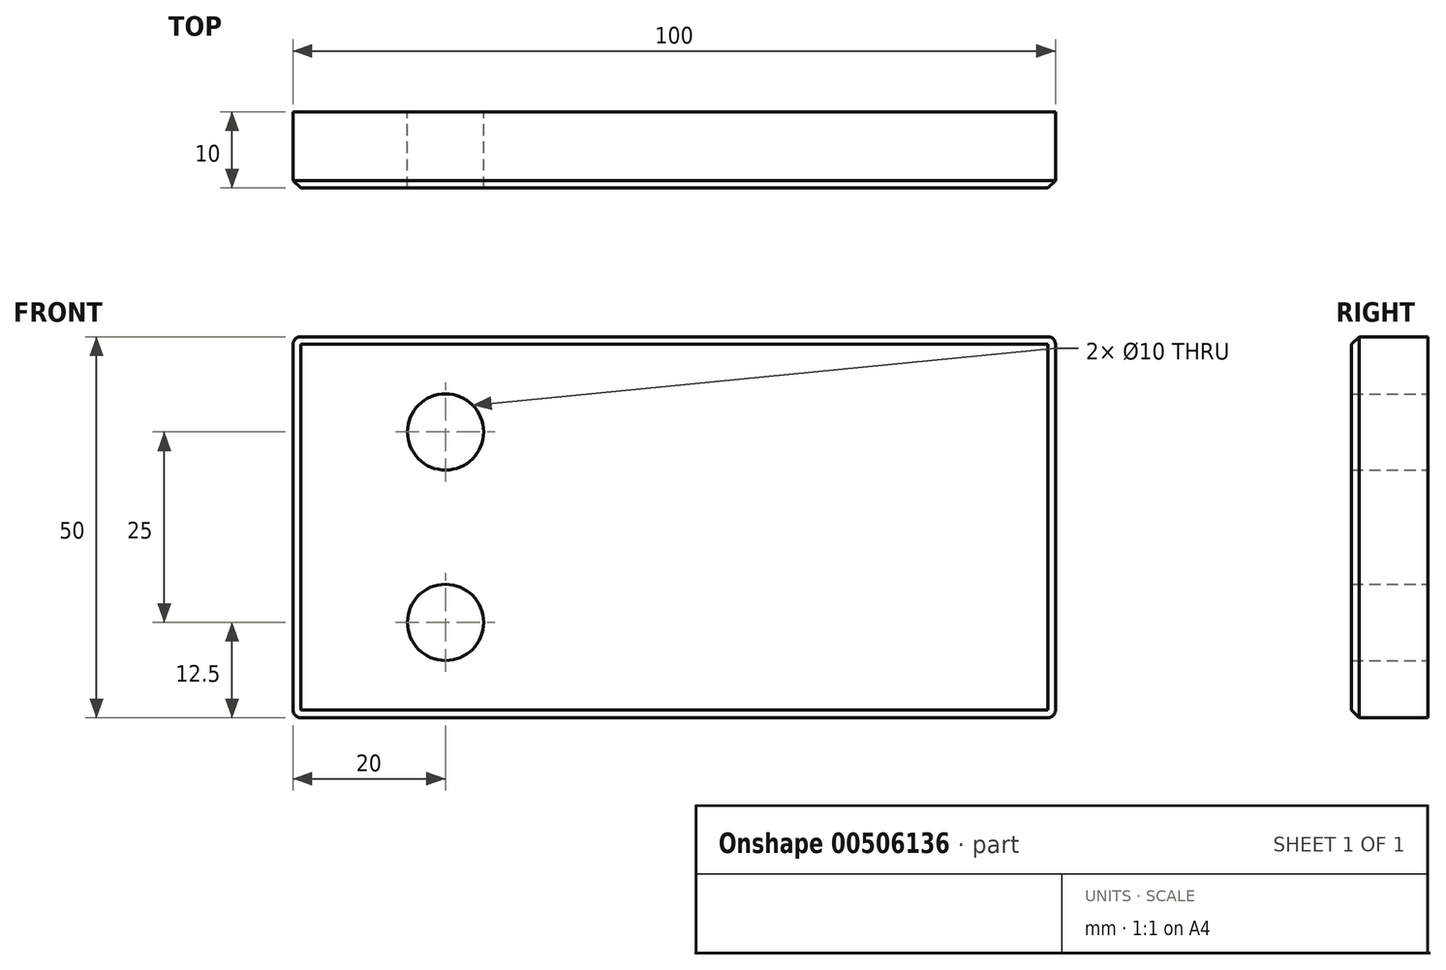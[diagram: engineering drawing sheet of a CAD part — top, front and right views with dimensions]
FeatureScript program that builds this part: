
annotation { "Feature Type Name" : "Feature", "Feature Type Description" : "" }
export const myFeature = defineFeature(function(context is Context, id is Id, definition is map)
    precondition{}
    {
        {
            var Q0;
            Q0=qCreatedBy(makeId("Front.planeOp"),FACE);
            var sketch = newSketch(context, id + "F0", { "sketchPlane" : qUnion([Q0])});
            skLineSegment(sketch, "E0.bottom", {"start": v(50, -25) * mm, "end": v(-50, -25) * mm});
            skLineSegment(sketch, "E0.top", {"start": v(50, 25) * mm, "end": v(-50, 25) * mm});
            skLineSegment(sketch, "E0.left", {"start": v(50, -25) * mm, "end": v(50, 25) * mm});
            skLineSegment(sketch, "E0.right", {"start": v(-50, -25) * mm, "end": v(-50, 25) * mm});
            skPoint(sketch, "E0.middle", {"position": v(0, 0) * mm});
            skCircle(sketch, "E1", {"center": v(-30, 12.5) * mm, "radius": 5 * mm});
            skCircle(sketch, "E2", {"center": v(-30, -12.5) * mm, "radius": 5 * mm});
            skSolve(sketch);
        }
        {
            var Q0;
            Q0=makeQuery(id+"F0.imprint","IMPRINT",FACE,{"disambiguationData":[TD([[makeQuery(id+"F0.imprint","IMPRINT",EDGE,{"derivedFrom":sQuery(id+"F0.wireOp",EDGE,"E0.bottom")}),-1.0]])]});
            extrude(context, id + "F1", {"entities" : qUnion([Q0]), "depth" : 10 * mm});
        }
        {
            var Q0;
            Q0=makeQuery(id+"F1.opExtrude","SWEPT_EDGE",EDGE,{"disambiguationData":[OSD([sQuery(id+"F0.wireOp",EDGE,"E0.bottom"),sQuery(id+"F0.wireOp",EDGE,"E0.left")])]});
            var Q1;
            Q1=makeQuery(id+"F1.opExtrude","SWEPT_EDGE",EDGE,{"disambiguationData":[OSD([sQuery(id+"F0.wireOp",EDGE,"E0.bottom"),sQuery(id+"F0.wireOp",EDGE,"E0.right")])]});
            var Q2;
            Q2=makeQuery(id+"F1.opExtrude","SWEPT_EDGE",EDGE,{"disambiguationData":[OSD([sQuery(id+"F0.wireOp",EDGE,"E0.top"),sQuery(id+"F0.wireOp",EDGE,"E0.right")])]});
            var Q3;
            Q3=makeQuery(id+"F1.opExtrude","SWEPT_EDGE",EDGE,{"disambiguationData":[OSD([sQuery(id+"F0.wireOp",EDGE,"E0.top"),sQuery(id+"F0.wireOp",EDGE,"E0.left")])]});
            fillet(context, id + "F2", {"entities" : qUnion([Q0, Q1, Q2, Q3]), "radius" : 1 * mm, "tangentPropagation" : true, "allowEdgeOverflow" : false});
        }
        {
            var Q0;
            Q0=makeQuery(id+"F1.opExtrude","CAP_EDGE",EDGE,{"disambiguationData":[OSD([sQuery(id+"F0.wireOp",EDGE,"E0.left")])],"isStart":false});
            var Q1;
            Q1=makeQuery(id+"F1.opExtrude","CAP_EDGE",EDGE,{"disambiguationData":[OSD([sQuery(id+"F0.wireOp",EDGE,"E0.bottom")])],"isStart":false});
            var Q2;
            Q2=makeQuery(id+"F1.opExtrude","CAP_EDGE",EDGE,{"disambiguationData":[OSD([sQuery(id+"F0.wireOp",EDGE,"E0.right")])],"isStart":false});
            var Q3;
            Q3=makeQuery(id+"F1.opExtrude","CAP_EDGE",EDGE,{"disambiguationData":[OSD([sQuery(id+"F0.wireOp",EDGE,"E0.top")])],"isStart":false});
            chamfer(context, id + "F3", {"entities" : qUnion([Q0, Q1, Q2, Q3]), "width" : 1 * mm, "tangentPropagation" : true});
        }
    });
